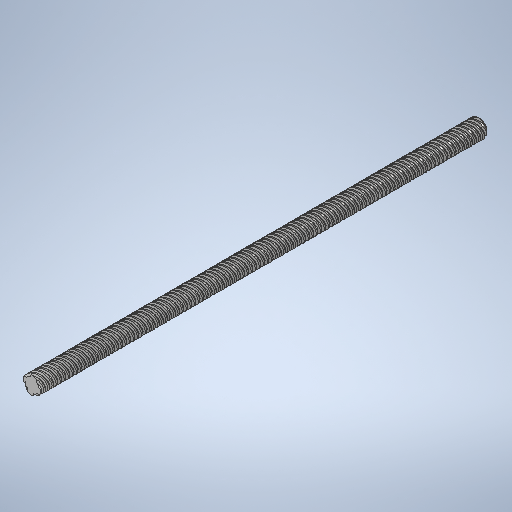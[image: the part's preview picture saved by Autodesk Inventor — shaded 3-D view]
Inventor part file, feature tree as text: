
AUTODESK INVENTOR PART (.ipt)
format: ipt  version: 2025.2 (Build 292293000, 293)  size: 1,698,304 bytes
history: native  units: mm
features: extrude x2, chamfer x1, other x1, pattern_circular x1, sketch x1
ambient origin geometry x8: Origin, YZ Plane, XZ Plane, XY Plane, X Axis, Y Axis, Z Axis, Center Point
bodies: Solid1 (feature_tree)
feature tree (6):
  extrude  "1000mm Rod"  Depth=0.907143mm TaperAngle=45.0deg
  chamfer  "Chamfer1"  Distance=7.257143mm
  other  "ACME Thread 2mm Pitch"
  pattern_circular  "4 Start"  Count=4 Angle=360.0deg
  extrude  "Extrusion2"  Depth=1.814286mm
  sketch  "Sketch3"  dims[d1=1000.0mm d2=0.0mm d3=0.907143mm d4=2.0mm d5=45.0deg d14=7.257143mm d15=1001.814286mm d16=10.0mm d17=0.0mm d18=90.0deg d19=90.0deg d20=0.0mm d21=0.0mm d40=40.0mm d41=360.0deg d43=1.814286mm d44=0.907143mm d48=5.061455mm d49=8.0mm d50=800.0mm d51=0.0mm]
